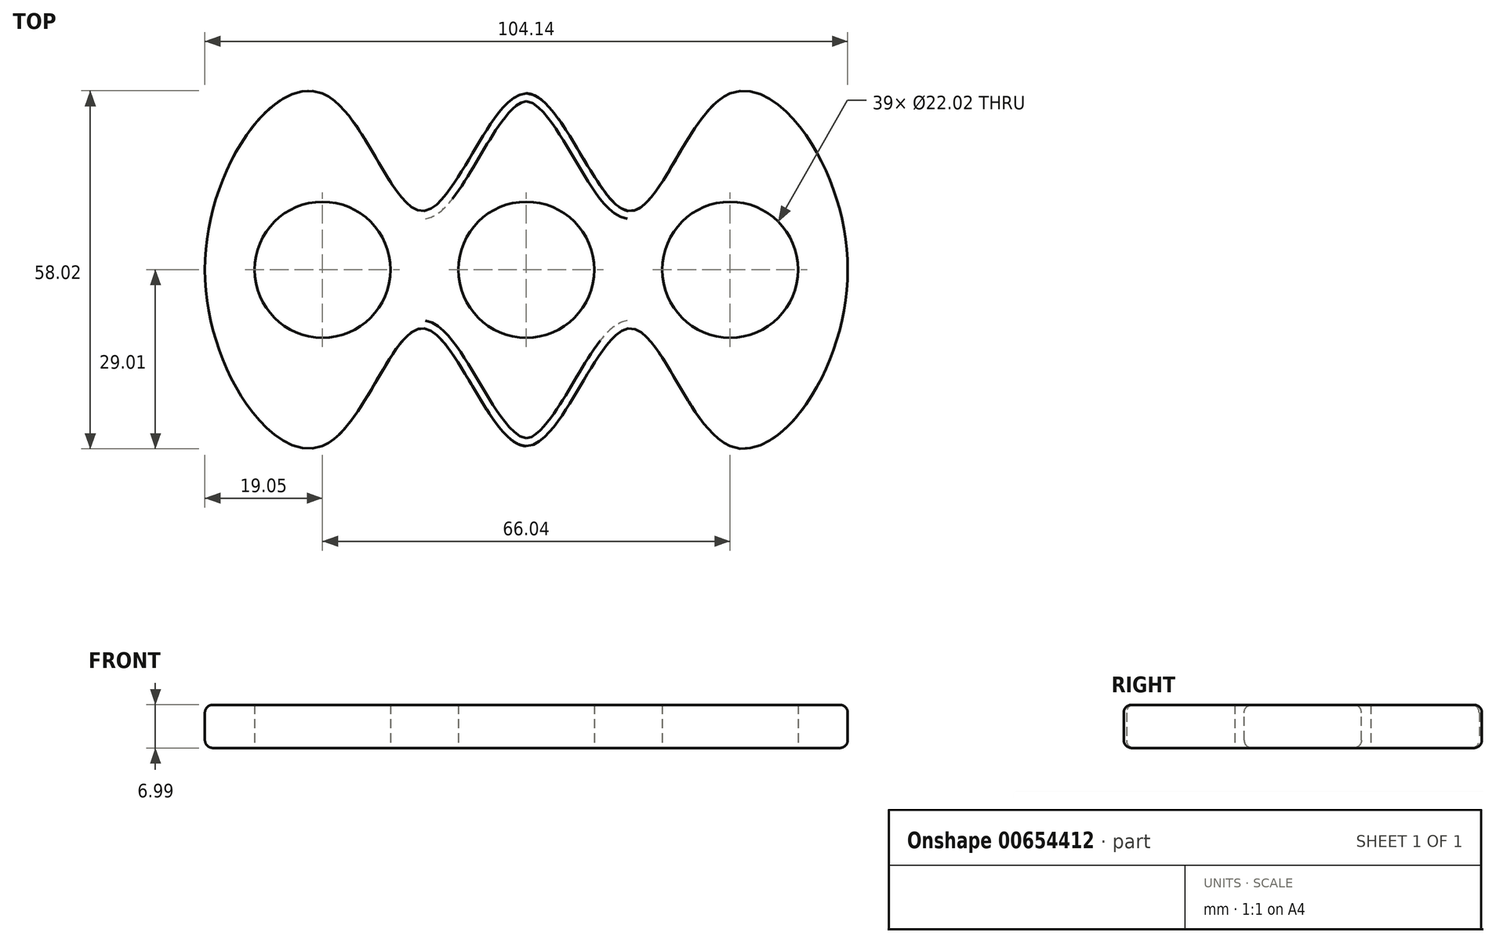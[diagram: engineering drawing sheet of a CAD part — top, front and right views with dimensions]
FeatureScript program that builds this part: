
annotation { "Feature Type Name" : "Feature", "Feature Type Description" : "" }
export const myFeature = defineFeature(function(context is Context, id is Id, definition is map)
    precondition{}
    {
        {
            var Q0;
            Q0=qCreatedBy(makeId("Top.planeOp"),FACE);
            var sketch = newSketch(context, id + "F0", { "sketchPlane" : qUnion([Q0])});
            skCircle(sketch, "E0", {"center": v(0, 0) * mm, "radius": 11.01 * mm});
            skCircle(sketch, "E1", {"center": v(33.02, 0) * mm, "radius": 11.01 * mm});
            skCircle(sketch, "E2", {"center": v(-33.02, 0) * mm, "radius": 11.01 * mm});
            skFitSpline(sketch, "E3", {"points": [v(0, 28.57) * mm, v(16.5, 9.53) * mm, v(33.02, 28.57) * mm, v(52.07, 0) * mm, v(33.02, -28.57) * mm, v(16.51, -9.53) * mm, v(0, -28.57) * mm, v(-16.51, -9.53) * mm, v(-33.02, -28.57) * mm, v(-52.07, 0) * mm, v(-33.02, 28.57) * mm, v(-16.51, 9.53) * mm, v(0, 28.57) * mm]});
            skPoint(sketch, "E4", {"position": v(-33.02, 28.58) * mm});
            skLineSegment(sketch, "E5", {"start": v(-33.02, 0) * mm, "end": v(0, 0) * mm});
            skLineSegment(sketch, "E6", {"start": v(0, 0) * mm, "end": v(33.02, 0) * mm});
            skPoint(sketch, "E7", {"position": v(-16.51, 0) * mm});
            skPoint(sketch, "E8", {"position": v(16.51, 0) * mm});
            skLineSegment(sketch, "E9", {"start": v(16.51, 9.53) * mm, "end": v(16.51, -9.53) * mm});
            skLineSegment(sketch, "E10", {"start": v(-16.51, 9.53) * mm, "end": v(-16.51, -9.53) * mm});
            skLineSegment(sketch, "E11", {"start": v(-52.07, 0) * mm, "end": v(-33.02, 0) * mm});
            skLineSegment(sketch, "E12", {"start": v(33.02, 0) * mm, "end": v(52.07, 0) * mm});
            skLineSegment(sketch, "E13", {"start": v(0, 28.58) * mm, "end": v(0, -28.58) * mm});
            skLineSegment(sketch, "E14", {"start": v(33.02, 28.58) * mm, "end": v(33.02, -28.58) * mm});
            skLineSegment(sketch, "E15", {"start": v(-33.02, 28.58) * mm, "end": v(-33.02, -28.58) * mm});
            skSolve(sketch);
        }
        {
            var Q0;
            Q0 = qSketchRegion(id + "F0", true);
            extrude(context, id + "F1", {"entities" : qUnion([Q0]), "depth" : 7 * mm, "offsetDistance" : 25.4 * mm});
        }
        {
            var Q0;
            Q0=makeQuery(id+"F1.opExtrude","CAP_EDGE",EDGE,{"disambiguationData":[OSD([sQuery(id+"F0.wireOp",EDGE,"E3")])],"isStart":false});
            var Q1;
            Q1=makeQuery(id+"F1.opExtrude","CAP_EDGE",EDGE,{"disambiguationData":[OSD([sQuery(id+"F0.wireOp",EDGE,"E3")])],"isStart":true});
            fillet(context, id + "F2", {"entities" : qUnion([Q0, Q1]), "radius" : 1.27 * mm, "tangentPropagation" : true, "allowEdgeOverflow" : false});
        }
    });
